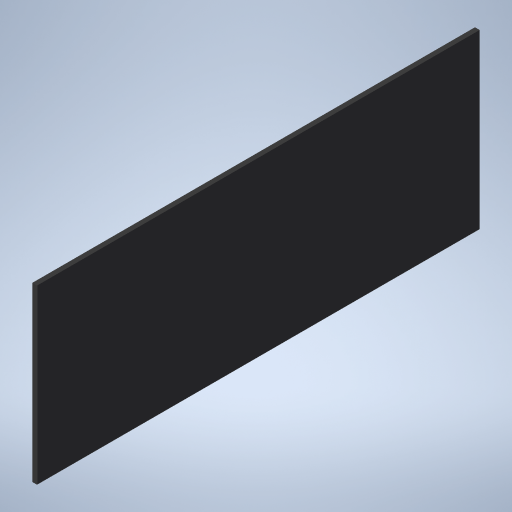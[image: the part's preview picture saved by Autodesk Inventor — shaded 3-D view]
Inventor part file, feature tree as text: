
AUTODESK INVENTOR PART (.ipt)
format: ipt  version: 2024.3 (Build 283343000, 343)  size: 201,728 bytes
history: native  units: mm
features: sheet_metal_op x1, sketch x1, other x1
ambient origin geometry x8: Origin, YZ Plane, XZ Plane, XY Plane, X Axis, Y Axis, Z Axis, Center Point
bodies: Solid1 (feature_tree)
feature tree (3):
  sheet_metal_op  "Face1"
  sketch  "Sketch1"  dims[d0=200.0mm d5=2.0mm d6=78.0mm]
  other  "Plate1"
